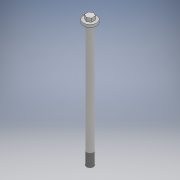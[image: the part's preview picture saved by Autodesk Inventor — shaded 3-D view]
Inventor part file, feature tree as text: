
AUTODESK INVENTOR PART (.ipt)
format: ipt  version: 2018 (Build 220112000, 112)  size: 111,104 bytes
history: native  units: mm
features: extrude x3, sketch x3, other x1, thread x1
ambient origin geometry x8: Origin, YZ Plane, XZ Plane, XY Plane, X Axis, Y Axis, Z Axis, Center Point
bodies: Body1 (feature_tree)
feature tree (8):
  other  "ソリッド1"
  extrude  "押し出し1"  Depth=11.9mm
  thread  "ねじ1"
  extrude  "押し出し2"  Depth=215.0mm TaperAngle=0.0deg
  extrude  "押し出し3"  Depth=22.0mm TaperAngle=0.0deg
  sketch  "スケッチ1"
  sketch  "スケッチ2"
  sketch  "スケッチ3"
